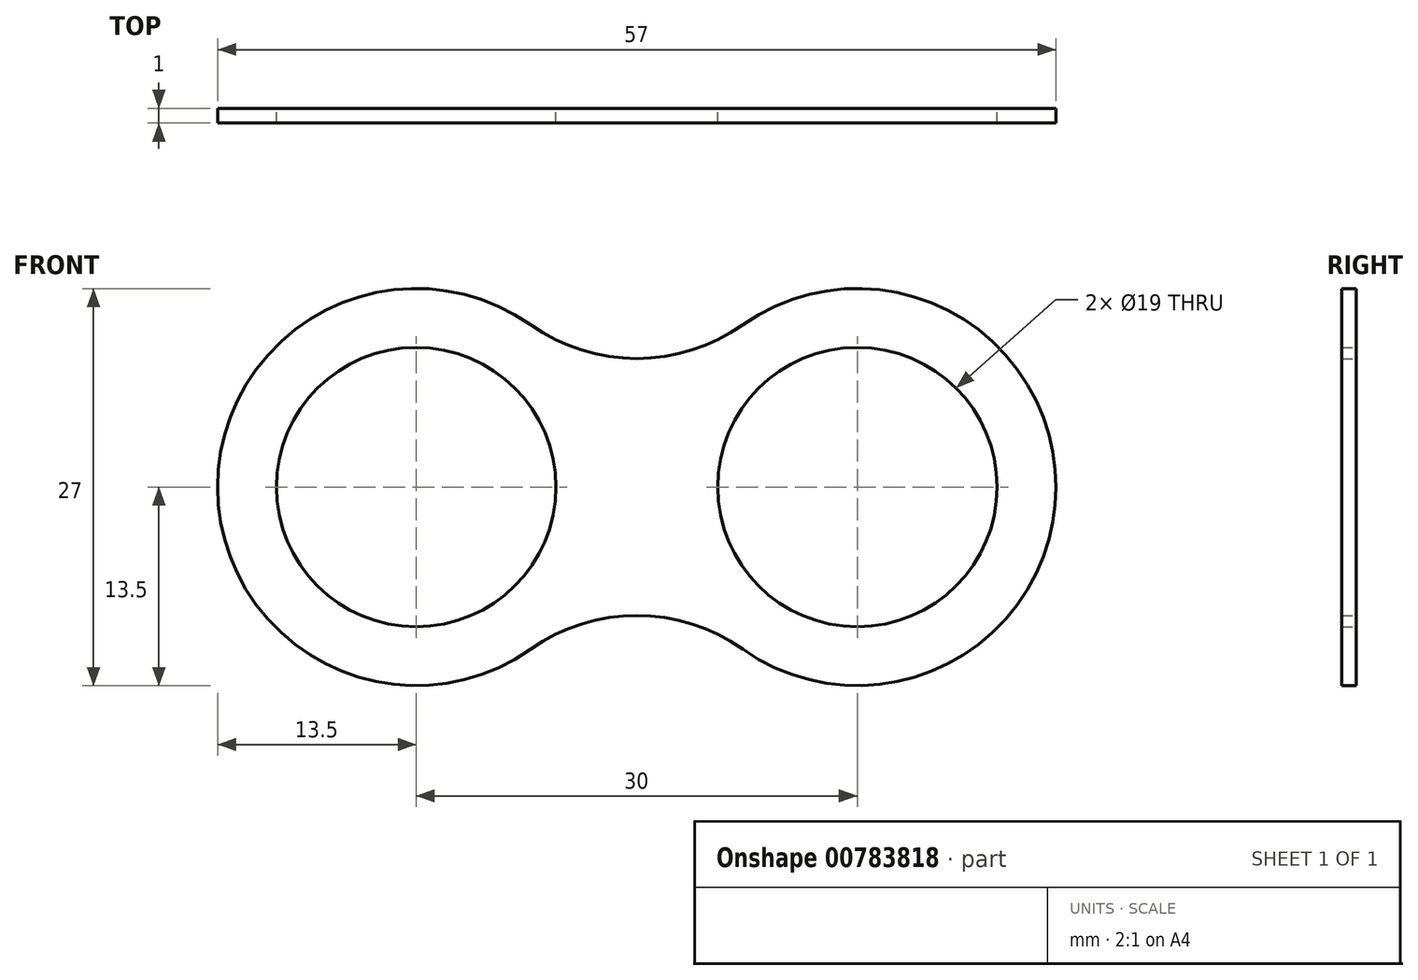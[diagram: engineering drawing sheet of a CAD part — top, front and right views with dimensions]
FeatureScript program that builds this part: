
annotation { "Feature Type Name" : "Feature", "Feature Type Description" : "" }
export const myFeature = defineFeature(function(context is Context, id is Id, definition is map)
    precondition{}
    {
        {
            var Q0;
            Q0=qCreatedBy(makeId("Front.planeOp"),FACE);
            var sketch = newSketch(context, id + "F0", { "sketchPlane" : qUnion([Q0])});
            skCircle(sketch, "E0", {"center": v(0, 0) * mm, "radius": 9.5 * mm});
            skArc(sketch, "E1", {"start": v(7.79, 11.03) * mm, "mid": v(-13.5, 0) * mm, "end": v(7.79, -11.03) * mm});
            skLineSegment(sketch, "E2", {"start": v(13.5, 0) * mm, "end": v(16.5, 0) * mm});
            skArc(sketch, "E3", {"start": v(22.21, -11.03) * mm, "mid": v(43.5, 0) * mm, "end": v(22.21, 11.03) * mm});
            skCircle(sketch, "E4", {"center": v(30, 0) * mm, "radius": 9.5 * mm});
            skArc(sketch, "E5", {"start": v(7.79, 11.03) * mm, "mid": v(15, 8.74) * mm, "end": v(22.21, 11.03) * mm});
            skPoint(sketch, "E5.first.point", {"position": v(7.79, 11.03) * mm});
            skPoint(sketch, "E5.second.point", {"position": v(22.21, 11.03) * mm});
            skPoint(sketch, "E5.third.point", {"position": v(19.88, 32.74) * mm});
            skArc(sketch, "E6", {"start": v(22.21, -11.03) * mm, "mid": v(15, -8.74) * mm, "end": v(7.79, -11.03) * mm});
            skPoint(sketch, "E6.first.point", {"position": v(7.79, -11.03) * mm});
            skPoint(sketch, "E6.second.point", {"position": v(22.21, -11.03) * mm});
            skPoint(sketch, "E6.third.point", {"position": v(13.5, -33.65) * mm});
            skSolve(sketch);
        }
        {
            var Q0;
            Q0=makeQuery(id+"F0.imprint","IMPRINT",FACE,{"disambiguationData":[TD([[makeQuery(id+"F0.imprint","IMPRINT",EDGE,{"derivedFrom":sQuery(id+"F0.wireOp",EDGE,"E0")}),-1.0]])]});
            extrude(context, id + "F1", {"entities" : qUnion([Q0]), "depth" : 1 * mm, "offsetDistance" : 25 * mm});
        }
    });
